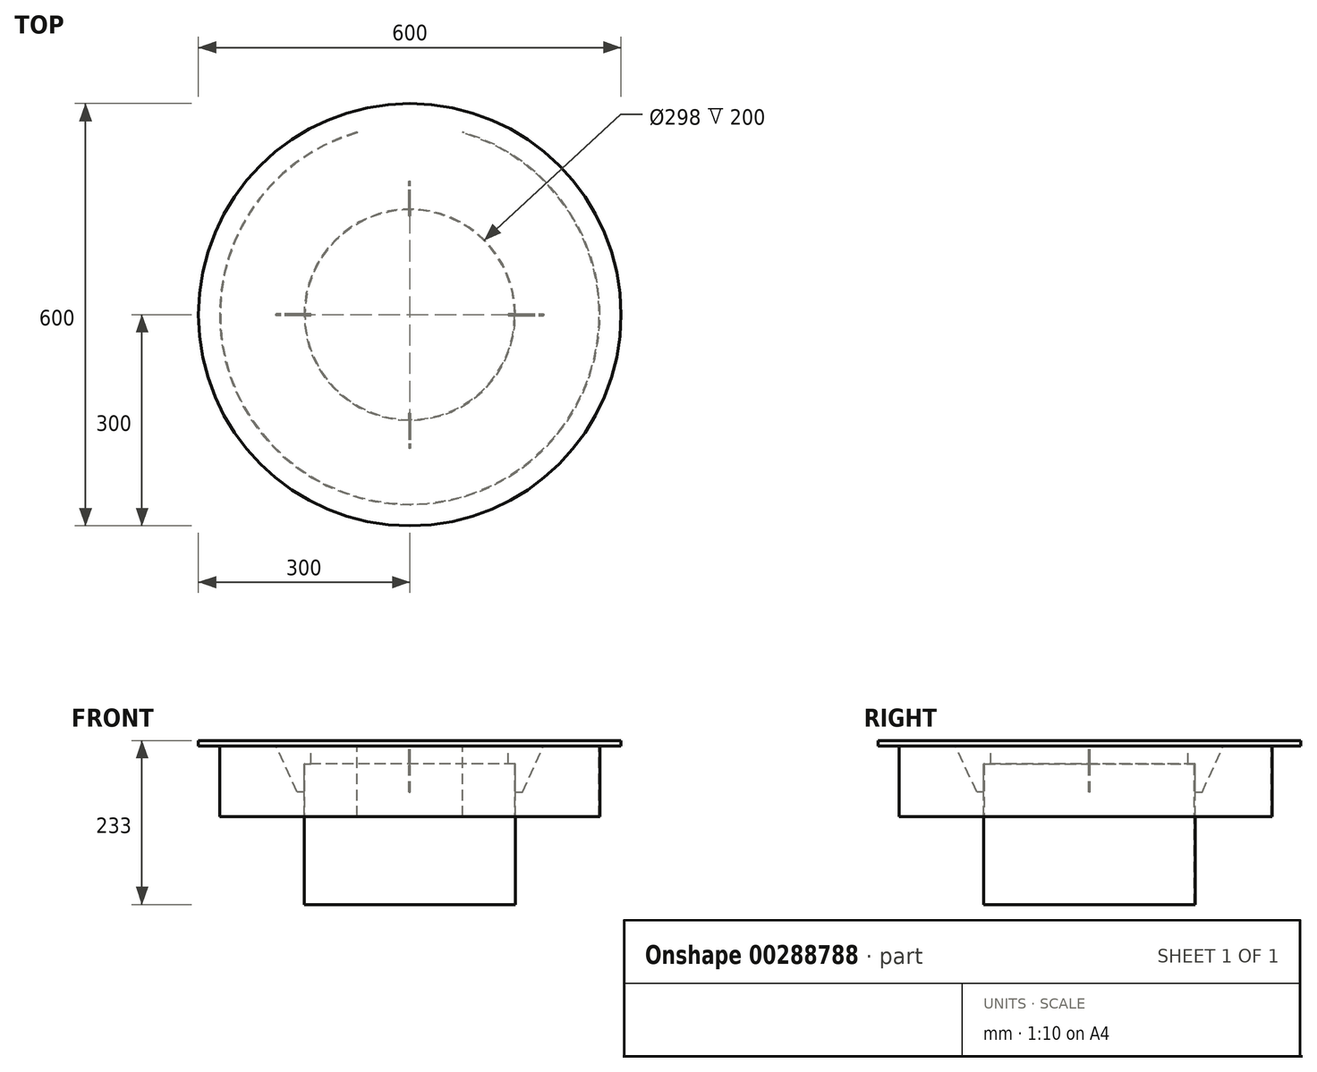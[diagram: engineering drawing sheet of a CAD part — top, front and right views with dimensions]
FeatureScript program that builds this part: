
annotation { "Feature Type Name" : "Feature", "Feature Type Description" : "" }
export const myFeature = defineFeature(function(context is Context, id is Id, definition is map)
    precondition{}
    {
        {
            assignVariable(context, id + "F0", {"name" : "TopThickness", "anyValue" : 8});
        }
        {
            var Q0;
            Q0=qCreatedBy(makeId("Top.planeOp"),FACE);
            var sketch = newSketch(context, id + "F1", { "sketchPlane" : qUnion([Q0])});
            skCircle(sketch, "E0", {"center": v(0, 0) * mm, "radius": 150 * mm});
            skCircle(sketch, "E1", {"center": v(0, 0) * mm, "radius": 149 * mm});
            skSolve(sketch);
        }
        {
            var Q0;
            Q0 = qSketchRegion(id + "F1", true);
            extrude(context, id + "F2", {"entities" : qUnion([Q0]), "oppositeDirection" : true, "depth" : 200 * mm});
        }
        {
            var Q0;
            Q0=qCreatedBy(makeId("Top.planeOp"),FACE);
            cPlane(context, id + "F3", {"entities" : qUnion([Q0]), "cplaneType" : CPlaneType.OFFSET, "offset" : 25 * mm, "width" : 150 * mm, "height" : 150 * mm});
        }
        {
            var Q0;
            Q0=qCreatedBy(id+"F3.planeOp",FACE);
            var sketch = newSketch(context, id + "F4", { "sketchPlane" : qUnion([Q0])});
            skCircle(sketch, "E2", {"center": v(0, 0) * mm, "radius": 300 * mm});
            skSolve(sketch);
        }
        {
            var Q0;
            Q0 = qSketchRegion(id + "F4", true);
            extrude(context, id + "F5", {"entities" : qUnion([Q0]), "depth" : (getVariable(context, 'TopThickness')) * mm});
        }
        {
            var Q0;
            Q0=qCreatedBy(makeId("Front.planeOp"),FACE);
            var sketch = newSketch(context, id + "F6", { "sketchPlane" : qUnion([Q0])});
            skLineSegment(sketch, "E3", {"start": v(-150, -40) * mm, "end": v(-150, 0) * mm});
            skLineSegment(sketch, "E4", {"start": v(-150, 0) * mm, "end": v(-140, 0) * mm});
            skLineSegment(sketch, "E5", {"start": v(-140, 0) * mm, "end": v(-140, 25) * mm});
            skLineSegment(sketch, "E6", {"start": v(-140, 25) * mm, "end": v(-190, 25) * mm});
            skLineSegment(sketch, "E7.0", {"start": v(-150, 0) * mm, "end": v(150, 0) * mm, "construction": true});
            skLineSegment(sketch, "E8", {"start": v(-150, -40) * mm, "end": v(-160, -40) * mm});
            skLineSegment(sketch, "E9", {"start": v(-160, -40) * mm, "end": v(-190, 25) * mm});
            skSolve(sketch);
        }
        {
            var Q0;
            Q0 = qSketchRegion(id + "F6", true);
            extrude(context, id + "F7", {"entities" : qUnion([Q0]), "depth" : 2 * mm, "symmetric" : true});
        }
        {
            var Q0;
            Q0=makeQuery(id+"F7.opExtrude","SWEPT_BODY",BODY,{"disambiguationData":[OSD([sQuery(id+"F6.wireOp",EDGE,"E3"),sQuery(id+"F6.wireOp",EDGE,"E4"),sQuery(id+"F6.wireOp",EDGE,"E5"),sQuery(id+"F6.wireOp",EDGE,"E6"),sQuery(id+"F6.wireOp",EDGE,"E8"),sQuery(id+"F6.wireOp",EDGE,"E9")])]});
            var Q1;
            Q1=makeQuery(id+"F2.opExtrude","CAP_EDGE",EDGE,{"disambiguationData":[OSD([sQuery(id+"F1.wireOp",EDGE,"E0")])],"isStart":false});
            circularPattern(context, id + "F8", {"entities" : qUnion([Q0]), "axis" : qUnion([Q1]), "angle" : 360 * degree, "instanceCount" : 4, "equalSpace" : true});
        }
        {
            var Q0;
            Q0=makeQuery(id+"F5.opExtrude","CAP_FACE",FACE,{"disambiguationData":[OSD([sQuery(id+"F4.wireOp",EDGE,"E2")])],"isStart":true});
            var sketch = newSketch(context, id + "F9", { "sketchPlane" : qUnion([Q0])});
            skArc(sketch, "E10.0", {"start": v(75, -259.37) * mm, "mid": v(0, 270) * mm, "end": v(-75, -259.37) * mm});
            skArc(sketch, "E11", {"start": v(75, -258.33) * mm, "mid": v(0, 269) * mm, "end": v(-75, -258.33) * mm});
            skLineSegment(sketch, "E12", {"start": v(75, -259.37) * mm, "end": v(75, -258.33) * mm});
            skLineSegment(sketch, "E13", {"start": v(-75, -259.37) * mm, "end": v(-75, -258.33) * mm});
            skSolve(sketch);
        }
        {
            var Q0;
            Q0 = qSketchRegion(id + "F9", true);
            extrude(context, id + "F10", {"entities" : qUnion([Q0]), "depth" : 100 * mm});
        }
    });
